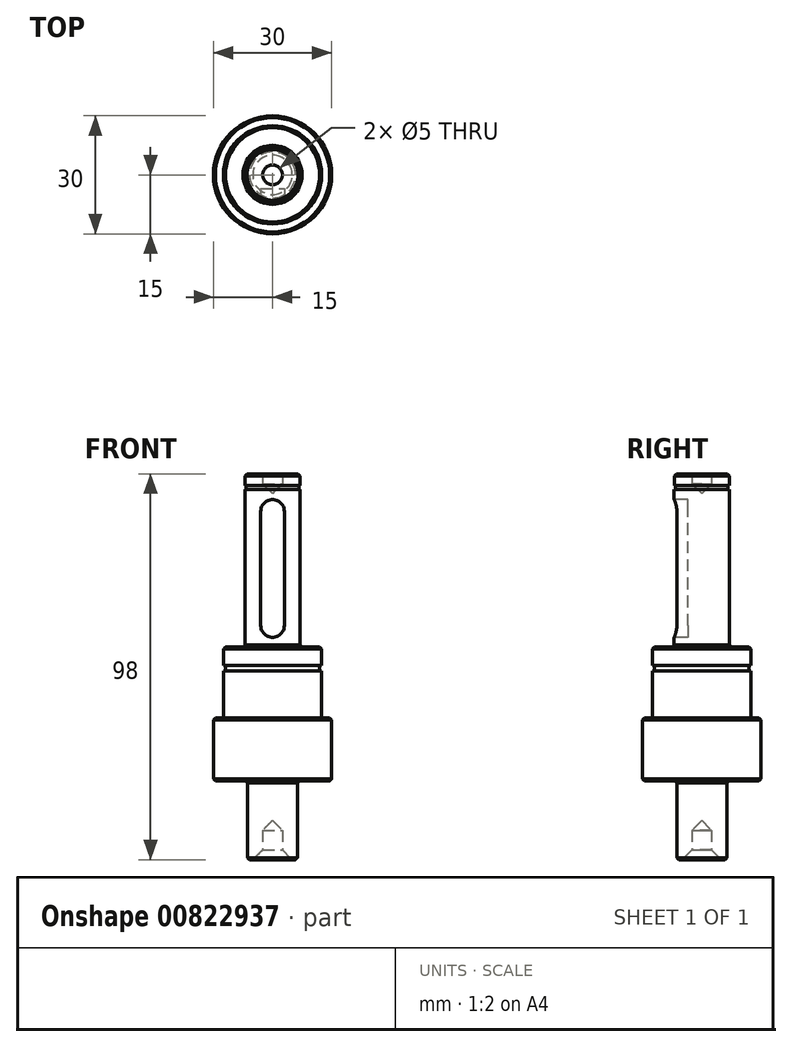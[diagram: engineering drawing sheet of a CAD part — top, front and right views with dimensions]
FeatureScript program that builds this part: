
annotation { "Feature Type Name" : "Feature", "Feature Type Description" : "" }
export const myFeature = defineFeature(function(context is Context, id is Id, definition is map)
    precondition{}
    {
        {
            var Q0;
            Q0=qCreatedBy(makeId("Front.planeOp"),FACE);
            var sketch = newSketch(context, id + "F0", { "sketchPlane" : qUnion([Q0])});
            skLineSegment(sketch, "E0", {"start": v(0, 0) * mm, "end": v(0, 15) * mm});
            skLineSegment(sketch, "E1", {"start": v(0, 15) * mm, "end": v(2.5, 17.5) * mm});
            skLineSegment(sketch, "E2", {"start": v(2.5, 17.5) * mm, "end": v(2.5, 20) * mm});
            skLineSegment(sketch, "E3", {"start": v(2.5, 20) * mm, "end": v(6.98, 20) * mm});
            skLineSegment(sketch, "E4", {"start": v(6.98, 20) * mm, "end": v(6.98, 17.1) * mm});
            skLineSegment(sketch, "E5", {"start": v(6.98, 17.1) * mm, "end": v(6.7, 17.1) * mm});
            skLineSegment(sketch, "E6", {"start": v(6.7, 17.1) * mm, "end": v(6.7, 16) * mm});
            skLineSegment(sketch, "E7", {"start": v(6.7, 16) * mm, "end": v(7, 16) * mm});
            skLineSegment(sketch, "E8", {"start": v(7, 16) * mm, "end": v(7, -24) * mm});
            skLineSegment(sketch, "E9", {"start": v(7, -24) * mm, "end": v(12.48, -24) * mm});
            skLineSegment(sketch, "E10", {"start": v(12.48, -24) * mm, "end": v(12.48, -28.7) * mm});
            skLineSegment(sketch, "E11", {"start": v(12.48, -28.7) * mm, "end": v(11.95, -28.7) * mm});
            skLineSegment(sketch, "E12", {"start": v(11.95, -28.7) * mm, "end": v(11.95, -30) * mm});
            skLineSegment(sketch, "E13", {"start": v(11.95, -30) * mm, "end": v(12.5, -30) * mm});
            skLineSegment(sketch, "E14", {"start": v(12.5, -30) * mm, "end": v(12.5, -42) * mm});
            skLineSegment(sketch, "E15", {"start": v(12.5, -42) * mm, "end": v(15, -42) * mm});
            skLineSegment(sketch, "E16", {"start": v(15, -42) * mm, "end": v(15, -58) * mm});
            skLineSegment(sketch, "E17", {"start": v(15, -58) * mm, "end": v(6.35, -58) * mm});
            skLineSegment(sketch, "E18", {"start": v(6.35, -58) * mm, "end": v(6.35, -78) * mm});
            skLineSegment(sketch, "E19", {"start": v(2.5, -75.5) * mm, "end": v(2.5, -70.5) * mm});
            skLineSegment(sketch, "E20", {"start": v(2.5, -70.5) * mm, "end": v(0, -68) * mm});
            skLineSegment(sketch, "E21", {"start": v(0, -68) * mm, "end": v(0, 0) * mm});
            skLineSegment(sketch, "E22", {"start": v(6.35, -78) * mm, "end": v(5, -78) * mm});
            skLineSegment(sketch, "E23", {"start": v(5, -78) * mm, "end": v(2.5, -75.5) * mm});
            skLineSegment(sketch, "E24", {"start": v(0, 15) * mm, "end": v(0, 95.93) * mm, "construction": true});
            skLineSegment(sketch, "E25", {"start": v(0, -68) * mm, "end": v(0, -104.42) * mm, "construction": true});
            skSolve(sketch);
        }
        {
            var Q0;
            Q0 = qSketchRegion(id + "F0", true);
            var Q1;
            Q1=sQuery(id+"F0.wireOp",EDGE,"E24");
            revolve(context, id + "F1", {"surfaceOperationType" : NewSurfaceOperationType.NEW, "entities" : qUnion([Q0]), "axis" : qUnion([Q1]), "revolveType" : RevolveType.FULL});
        }
        {
            var Q0;
            Q0=makeQuery(id+"F1.opRevolve","SWEPT_EDGE",EDGE,{"disambiguationData":[OSD([sQuery(id+"F0.wireOp",EDGE,"E3"),sQuery(id+"F0.wireOp",EDGE,"E4")])]});
            var Q1;
            Q1=makeQuery(id+"F1.opRevolve","SWEPT_FACE",FACE,{"disambiguationData":[OSD([sQuery(id+"F0.wireOp",EDGE,"E9")])]});
            var Q2;
            Q2=makeQuery(id+"F1.opRevolve","SWEPT_FACE",FACE,{"disambiguationData":[OSD([sQuery(id+"F0.wireOp",EDGE,"E17")])]});
            var Q3;
            Q3=makeQuery(id+"F1.opRevolve","SWEPT_EDGE",EDGE,{"disambiguationData":[OSD([sQuery(id+"F0.wireOp",EDGE,"E18"),sQuery(id+"F0.wireOp",EDGE,"E22")])]});
            var Q4;
            Q4=makeQuery(id+"F1.opRevolve","SWEPT_EDGE",EDGE,{"disambiguationData":[OSD([sQuery(id+"F0.wireOp",EDGE,"E15"),sQuery(id+"F0.wireOp",EDGE,"E16")])]});
            chamfer(context, id + "F2", {"entities" : qUnion([Q0, Q1, Q2, Q3, Q4]), "width" : 0.5 * mm, "tangentPropagation" : true});
        }
        {
            var Q0;
            Q0=makeQuery(id+"F1.opRevolve","SWEPT_EDGE",EDGE,{"disambiguationData":[OSD([sQuery(id+"F0.wireOp",EDGE,"E14"),sQuery(id+"F0.wireOp",EDGE,"E15")])]});
            fillet(context, id + "F3", {"entities" : qUnion([Q0]), "radius" : 0.5 * mm, "tangentPropagation" : true, "allowEdgeOverflow" : false});
        }
        {
            var Q0;
            Q0=qCreatedBy(makeId("Front.planeOp"),FACE);
            cPlane(context, id + "F4", {"entities" : qUnion([Q0]), "cplaneType" : CPlaneType.OFFSET, "offset" : 7 * mm, "width" : 150 * mm, "height" : 150 * mm});
        }
        {
            var Q0;
            Q0=qCreatedBy(id+"F4.planeOp",FACE);
            var sketch = newSketch(context, id + "F5", { "sketchPlane" : qUnion([Q0])});
            skLineSegment(sketch, "E26", {"start": v(0, 0) * mm, "end": v(0, 10.5) * mm, "construction": true});
            skLineSegment(sketch, "E27", {"start": v(0, -18.5) * mm, "end": v(0, 0) * mm, "construction": true});
            skArc(sketch, "E28", {"start": v(3, 10.5) * mm, "mid": v(0, 13.5) * mm, "end": v(-3, 10.5) * mm});
            skArc(sketch, "E29", {"start": v(-3, -18.5) * mm, "mid": v(0, -21.5) * mm, "end": v(3, -18.5) * mm});
            skLineSegment(sketch, "E30.0", {"start": v(7, 16) * mm, "end": v(-7, 16) * mm, "construction": true});
            skLineSegment(sketch, "E30.1", {"start": v(-11.98, -24) * mm, "end": v(11.98, -24) * mm, "construction": true});
            skLineSegment(sketch, "E31", {"start": v(3, -18.5) * mm, "end": v(3, 10.5) * mm});
            skLineSegment(sketch, "E32", {"start": v(-3, 10.5) * mm, "end": v(-3, -18.5) * mm});
            skSolve(sketch);
        }
        {
            var Q0;
            Q0 = qSketchRegion(id + "F5", true);
            extrude(context, id + "F6", {"entities" : qUnion([Q0]), "operationType" : NewBodyOperationType.REMOVE, "oppositeDirection" : true, "depth" : 3.5 * mm, "offsetDistance" : 25 * mm});
        }
    });
